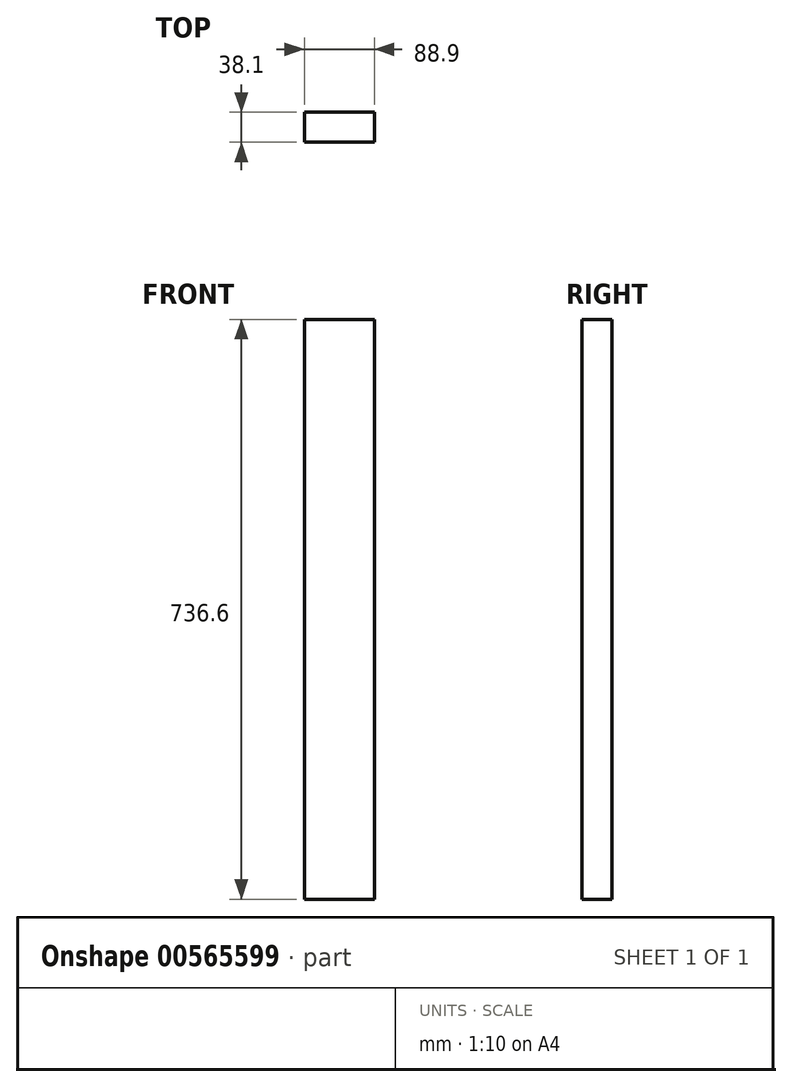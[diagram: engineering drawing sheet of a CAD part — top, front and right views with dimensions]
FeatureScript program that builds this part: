
annotation { "Feature Type Name" : "Feature", "Feature Type Description" : "" }
export const myFeature = defineFeature(function(context is Context, id is Id, definition is map)
    precondition{}
    {
        {
            var Q0;
            Q0=qCreatedBy(makeId("Top.planeOp"),FACE);
            var sketch = newSketch(context, id + "F0", { "sketchPlane" : qUnion([Q0])});
            skLineSegment(sketch, "E0.bottom", {"start": v(0, 0) * mm, "end": v(88.9, 0) * mm});
            skLineSegment(sketch, "E0.top", {"start": v(0, 38.1) * mm, "end": v(88.9, 38.1) * mm});
            skLineSegment(sketch, "E0.left", {"start": v(0, 0) * mm, "end": v(0, 38.1) * mm});
            skLineSegment(sketch, "E0.right", {"start": v(88.9, 0) * mm, "end": v(88.9, 38.1) * mm});
            skSolve(sketch);
        }
        {
            var Q0;
            Q0=qSketchRegion(id+"F0",true);
            extrude(context, id + "F1", {"entities" : qUnion([Q0]), "depth" : 914.4 * mm - 177.8 * mm, "offsetDistance" : 25.4 * mm});
        }
    });
